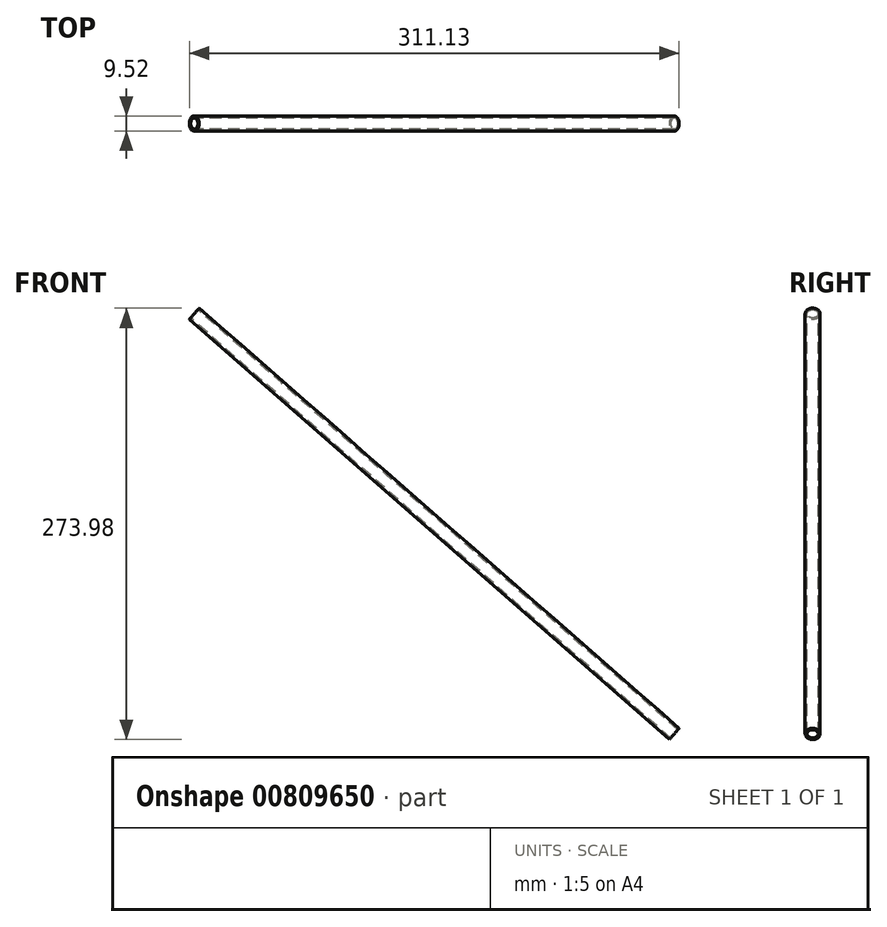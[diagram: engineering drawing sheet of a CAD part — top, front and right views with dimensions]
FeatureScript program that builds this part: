
annotation { "Feature Type Name" : "Feature", "Feature Type Description" : "" }
export const myFeature = defineFeature(function(context is Context, id is Id, definition is map)
    precondition{}
    {
        {
            var Q0;
            Q0=qCreatedBy(makeId("Right.planeOp"),FACE);
            cPlane(context, id + "F0", {"entities" : qUnion([Q0]), "cplaneType" : CPlaneType.OFFSET, "offset" : 233.43 * mm, "oppositeDirection" : true, "width" : 152.4 * mm, "height" : 152.4 * mm});
        }
        {
            var Q0;
            Q0=qCreatedBy(id+"F0.planeOp",FACE);
            var sketch = newSketch(context, id + "F1", { "sketchPlane" : qUnion([Q0])});
            skPoint(sketch, "E0", {"position": v(0, 0) * mm});
            skPoint(sketch, "E1", {"position": v(127, 0) * mm});
            skPoint(sketch, "E2", {"position": v(-127, 0) * mm});
            skSolve(sketch);
        }
        {
            var Q0;
            Q0=qCreatedBy(makeId("Right.planeOp"),FACE);
            var sketch = newSketch(context, id + "F2", { "sketchPlane" : qUnion([Q0])});
            skPoint(sketch, "E3", {"position": v(0, 266.7) * mm});
            skSolve(sketch);
        }
        {
            var Q0;
            Q0=sQuery(id+"F2.wireOp",VERTEX,"E3");
            var Q1;
            Q1=sQuery(id+"F1.wireOp",VERTEX,"E2");
            var Q2;
            Q2=sQuery(id+"F1.wireOp",VERTEX,"E1");
            cPlane(context, id + "F3", {"entities" : qUnion([Q0, Q1, Q2]), "cplaneType" : CPlaneType.THREE_POINT, "offset" : 25.4 * mm, "width" : 152.4 * mm, "height" : 152.4 * mm});
        }
        {
            var Q0;
            Q0=qCreatedBy(id+"F3.planeOp",FACE);
            var sketch = newSketch(context, id + "F4", { "sketchPlane" : qUnion([Q0])});
            skCircle(sketch, "E4", {"center": v(0, 200.85) * mm, "radius": 4.76 * mm});
            skCircle(sketch, "E5", {"center": v(0, 200.85) * mm, "radius": 3.52 * mm});
            skSolve(sketch);
        }
        {
            var Q0;
            Q0=makeQuery(id+"F4.imprint","IMPRINT",FACE,{"disambiguationData":[TD([[makeQuery(id+"F4.imprint","IMPRINT",EDGE,{"derivedFrom":sQuery(id+"F4.wireOp",EDGE,"E4")}),1.0]])]});
            extrude(context, id + "F5", {"entities" : qUnion([Q0]), "oppositeDirection" : true, "depth" : 405.13 * mm, "offsetDistance" : 25.4 * mm});
        }
    });
